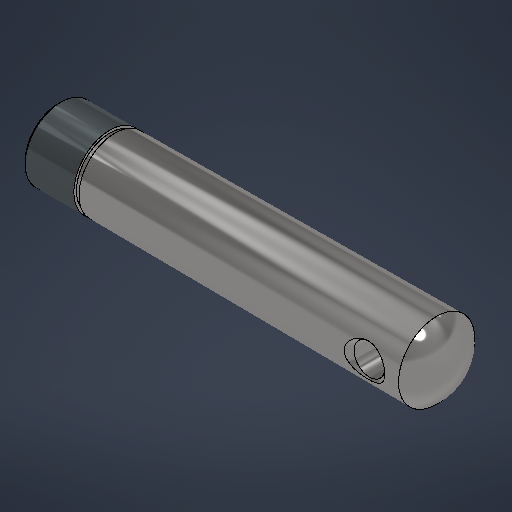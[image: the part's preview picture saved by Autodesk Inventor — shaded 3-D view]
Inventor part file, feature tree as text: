
AUTODESK INVENTOR PART (.ipt)
format: ipt  version: 2025.3 (Build 293356000, 356)  size: 302,080 bytes
history: native  units: mm
features: sketch x3, revolve x2, hole x1, extrude x1, mirror x1, chamfer x1
ambient origin geometry x8: Origin, YZ Plane, XZ Plane, XY Plane, X Axis, Y Axis, Z Axis, Center Point
bodies: Solid1 (feature_tree)
feature tree (9):
  sketch  "Sketch1"  dims[d4=0.066323mm d5=10.2mm]
  revolve  "Revolution1"  [1 undecoded]
  hole  "Hole1"  [1 undecoded]
  extrude  "Extrusion1"  TaperAngle=60.0deg  [1 undecoded]
  revolve  "Revolution2"  [1 undecoded]
  mirror  "Mirror1"
  chamfer  "Chamfer1"  Distance=77.0mm
  sketch  "Sketch2"  dims[d6=14.0mm d7=14.0mm]
  sketch  "Sketch3"  dims[d11=50.0mm d13=60.0deg d19=10.0mm d20=77.0mm d21=67.0mm d22=6.0mm d23=0.5mm d24=10.0mm d25=1.0mm d26=360.0deg d27=0.0mm d28=0.0mm d29=45.0deg d30=1.0mm d31=90.0deg d32=14.83181mm d35=10.106mm d36=35.0mm d37=4.0mm d38=2.0mm d39=90.0deg d40=50.0mm d41=120.0deg d42=0.5mm d43=2.0mm d44=45.0deg]
note: 4 required parameter values undecoded (feature->parameter linkage not recoverable at this tier; creation-order binding heuristic only, values carry confidence <= 0.55)